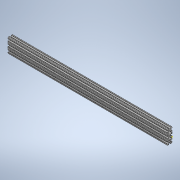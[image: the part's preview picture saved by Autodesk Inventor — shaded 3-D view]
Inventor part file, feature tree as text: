
AUTODESK INVENTOR PART (.ipt)
format: ipt  version: 2020 (Build 240168000, 168)  size: 392,704 bytes
history: native  units: in
note: dims shown in document units (in); Inventor stores cm internally (conversion verified against a paired STEP export)
features: sketch x2, extrude x1
ambient origin geometry x8: Origin, YZ Plane, XZ Plane, XY Plane, X Axis, Y Axis, Z Axis, Center Point
bodies: Solid1 (feature_tree)
feature tree (3):
  extrude  "Extrusion1"  [1 undecoded]
  sketch  "Sketch2"
  sketch  "Sketch1"  dims[d0=33.0in d1=0.0in]
note: 1 required parameter value undecoded (feature->parameter linkage not recoverable at this tier; creation-order binding heuristic only, values carry confidence <= 0.55)
